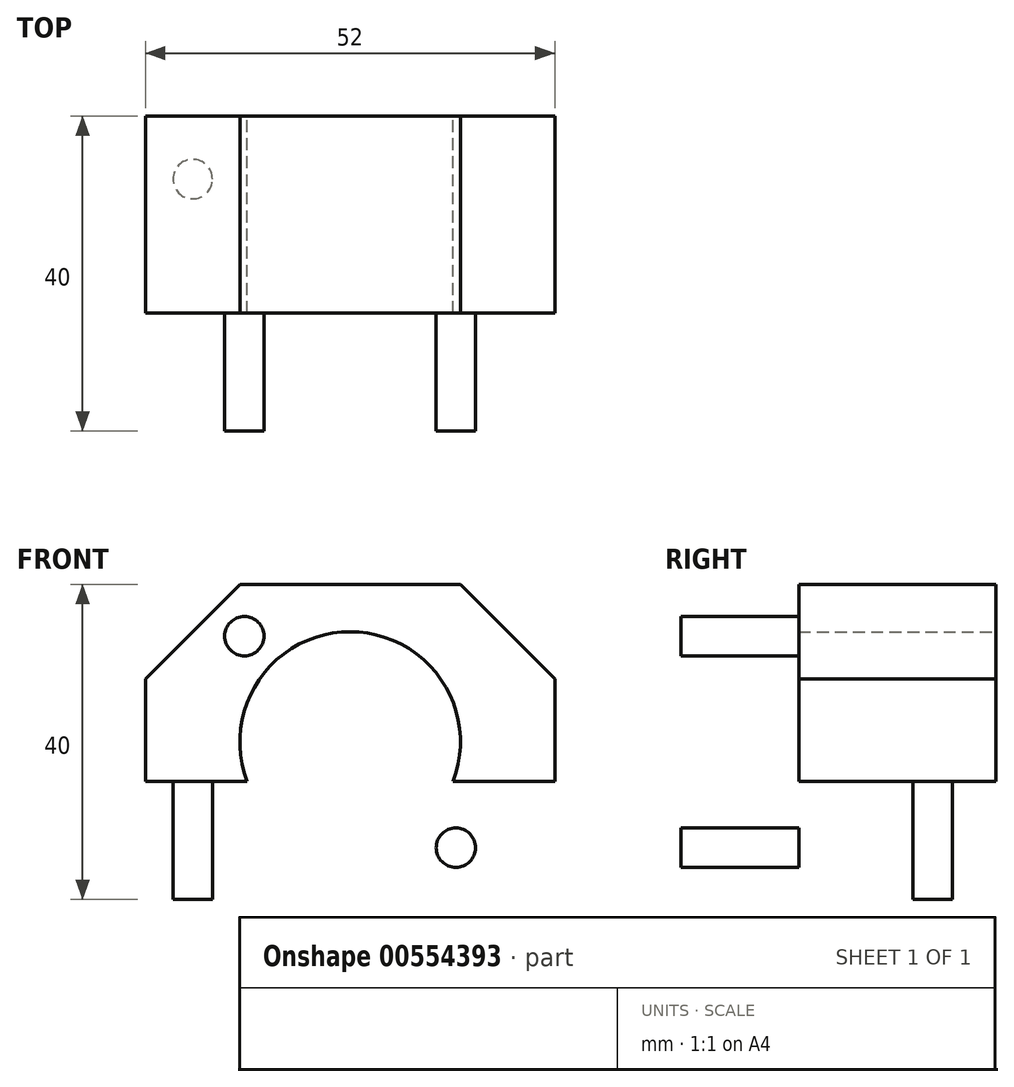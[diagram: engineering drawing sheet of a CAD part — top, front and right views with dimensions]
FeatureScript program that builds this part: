
annotation { "Feature Type Name" : "Feature", "Feature Type Description" : "" }
export const myFeature = defineFeature(function(context is Context, id is Id, definition is map)
    precondition{}
    {
        {
            var Q0;
            Q0=qCreatedBy(makeId("Front.planeOp"),FACE);
            var sketch = newSketch(context, id + "F0", { "sketchPlane" : qUnion([Q0])});
            skLineSegment(sketch, "E0.bottom", {"start": v(0, 0) * mm, "end": v(52, 0) * mm});
            skLineSegment(sketch, "E0.top", {"start": v(0, 40) * mm, "end": v(52, 40) * mm});
            skLineSegment(sketch, "E0.left", {"start": v(0, 0) * mm, "end": v(0, 40) * mm});
            skLineSegment(sketch, "E0.right", {"start": v(52, 0) * mm, "end": v(52, 40) * mm});
            skLineSegment(sketch, "E1", {"start": v(26, 40) * mm, "end": v(26, 0) * mm, "construction": true});
            skLineSegment(sketch, "E2", {"start": v(0, 20) * mm, "end": v(52, 20) * mm, "construction": true});
            skLineSegment(sketch, "E3", {"start": v(0, 28) * mm, "end": v(12, 40) * mm});
            skLineSegment(sketch, "E4.MirrorCS", {"start": v(52, 28) * mm, "end": v(40, 40) * mm});
            skCircle(sketch, "E5", {"center": v(26, 20) * mm, "radius": 14 * mm});
            skSolve(sketch);
        }
        {
            var Q0;
            {var subQ1=sQuery(id+"F0.wireOp",EDGE,"E0.bottom");Q0=makeQuery(id+"F0.imprint","IMPRINT",FACE,{"disambiguationData":[TD([[makeQuery(id+"F0.imprint","IMPRINT",EDGE,{"derivedFrom":subQ1}),1.0]])]});}
            extrude(context, id + "F1", {"entities" : qUnion([Q0]), "depth" : 40 * mm, "offsetDistance" : 25 * mm});
        }
        {
            var Q0;
            Q0=makeQuery(id+"F1.opExtrude","CAP_FACE",FACE,{"disambiguationData":[OSD([sQuery(id+"F0.wireOp",EDGE,"E0.bottom"),sQuery(id+"F0.wireOp",EDGE,"E0.top"),sQuery(id+"F0.wireOp",EDGE,"E0.left"),sQuery(id+"F0.wireOp",EDGE,"E0.right"),sQuery(id+"F0.wireOp",EDGE,"E3"),sQuery(id+"F0.wireOp",EDGE,"E4.MirrorCS"),sQuery(id+"F0.wireOp",EDGE,"E5")])],"isStart":false});
            var sketch = newSketch(context, id + "F2", { "sketchPlane" : qUnion([Q0])});
            skCircle(sketch, "E6", {"center": v(45, 20) * mm, "radius": 2.5 * mm});
            skCircle(sketch, "E7", {"center": v(7, 20) * mm, "radius": 2.5 * mm});
            skCircle(sketch, "E8", {"center": v(39.44, 33.44) * mm, "radius": 2.5 * mm});
            skCircle(sketch, "E9.MirrorC", {"center": v(39.44, 6.56) * mm, "radius": 2.5 * mm});
            skCircle(sketch, "E10.MirrorC", {"center": v(12.56, 33.44) * mm, "radius": 2.5 * mm});
            skCircle(sketch, "E11.MirrorC", {"center": v(12.56, 6.56) * mm, "radius": 2.5 * mm});
            skSolve(sketch);
        }
        {
            var Q0;
            Q0=makeQuery(id+"F2.imprint","IMPRINT",FACE,{"disambiguationData":[TD([[makeQuery(id+"F2.imprint","IMPRINT",EDGE,{"derivedFrom":sQuery(id+"F2.wireOp",EDGE,"E8")}),1.0]])]});
            var Q1;
            Q1=makeQuery(id+"F2.imprint","IMPRINT",FACE,{"disambiguationData":[TD([[makeQuery(id+"F2.imprint","IMPRINT",EDGE,{"derivedFrom":sQuery(id+"F2.wireOp",EDGE,"E6")}),1.0]])]});
            var Q2;
            Q2=makeQuery(id+"F2.imprint","IMPRINT",FACE,{"disambiguationData":[TD([[makeQuery(id+"F2.imprint","IMPRINT",EDGE,{"derivedFrom":sQuery(id+"F2.wireOp",EDGE,"E9.MirrorC")}),-1.0]])]});
            var Q3;
            Q3=makeQuery(id+"F2.imprint","IMPRINT",FACE,{"disambiguationData":[TD([[makeQuery(id+"F2.imprint","IMPRINT",EDGE,{"derivedFrom":sQuery(id+"F2.wireOp",EDGE,"E11.MirrorC")}),1.0]])]});
            var Q4;
            Q4=makeQuery(id+"F2.imprint","IMPRINT",FACE,{"disambiguationData":[TD([[makeQuery(id+"F2.imprint","IMPRINT",EDGE,{"derivedFrom":sQuery(id+"F2.wireOp",EDGE,"E7")}),1.0]])]});
            var Q5;
            Q5=makeQuery(id+"F2.imprint","IMPRINT",FACE,{"disambiguationData":[TD([[makeQuery(id+"F2.imprint","IMPRINT",EDGE,{"derivedFrom":sQuery(id+"F2.wireOp",EDGE,"E10.MirrorC")}),-1.0]])]});
            extrude(context, id + "F3", {"entities" : qUnion([Q0, Q1, Q2, Q3, Q4, Q5]), "operationType" : NewBodyOperationType.REMOVE, "oppositeDirection" : true, "depth" : 15 * mm, "offsetDistance" : 25 * mm});
        }
        {
            var Q0;
            Q0=makeQuery(id+"F1.opExtrude","SWEPT_FACE",FACE,{"disambiguationData":[OSD([sQuery(id+"F0.wireOp",EDGE,"E0.bottom")])]});
            var sketch = newSketch(context, id + "F4", { "sketchPlane" : qUnion([Q0])});
            skCircle(sketch, "E12", {"center": v(46, 32) * mm, "radius": 2.5 * mm});
            skCircle(sketch, "E13", {"center": v(46, 8) * mm, "radius": 2.5 * mm});
            skCircle(sketch, "E14.MirrorC", {"center": v(6, 32) * mm, "radius": 2.5 * mm});
            skCircle(sketch, "E15.MirrorC", {"center": v(6, 8) * mm, "radius": 2.5 * mm});
            skSolve(sketch);
        }
        {
            var Q0;
            Q0=makeQuery(id+"F4.imprint","IMPRINT",FACE,{"disambiguationData":[TD([[makeQuery(id+"F4.imprint","IMPRINT",EDGE,{"derivedFrom":sQuery(id+"F4.wireOp",EDGE,"E12")}),1.0]])]});
            var Q1;
            Q1=makeQuery(id+"F4.imprint","IMPRINT",FACE,{"disambiguationData":[TD([[makeQuery(id+"F4.imprint","IMPRINT",EDGE,{"derivedFrom":sQuery(id+"F4.wireOp",EDGE,"E13")}),1.0]])]});
            var Q2;
            Q2=makeQuery(id+"F4.imprint","IMPRINT",FACE,{"disambiguationData":[TD([[makeQuery(id+"F4.imprint","IMPRINT",EDGE,{"derivedFrom":sQuery(id+"F4.wireOp",EDGE,"E15.MirrorC")}),-1.0]])]});
            var Q3;
            Q3=makeQuery(id+"F4.imprint","IMPRINT",FACE,{"disambiguationData":[TD([[makeQuery(id+"F4.imprint","IMPRINT",EDGE,{"derivedFrom":sQuery(id+"F4.wireOp",EDGE,"E14.MirrorC")}),-1.0]])]});
            extrude(context, id + "F5", {"entities" : qUnion([Q0, Q1, Q2, Q3]), "operationType" : NewBodyOperationType.REMOVE, "oppositeDirection" : true, "depth" : 15 * mm, "offsetDistance" : 25 * mm});
        }
    });
